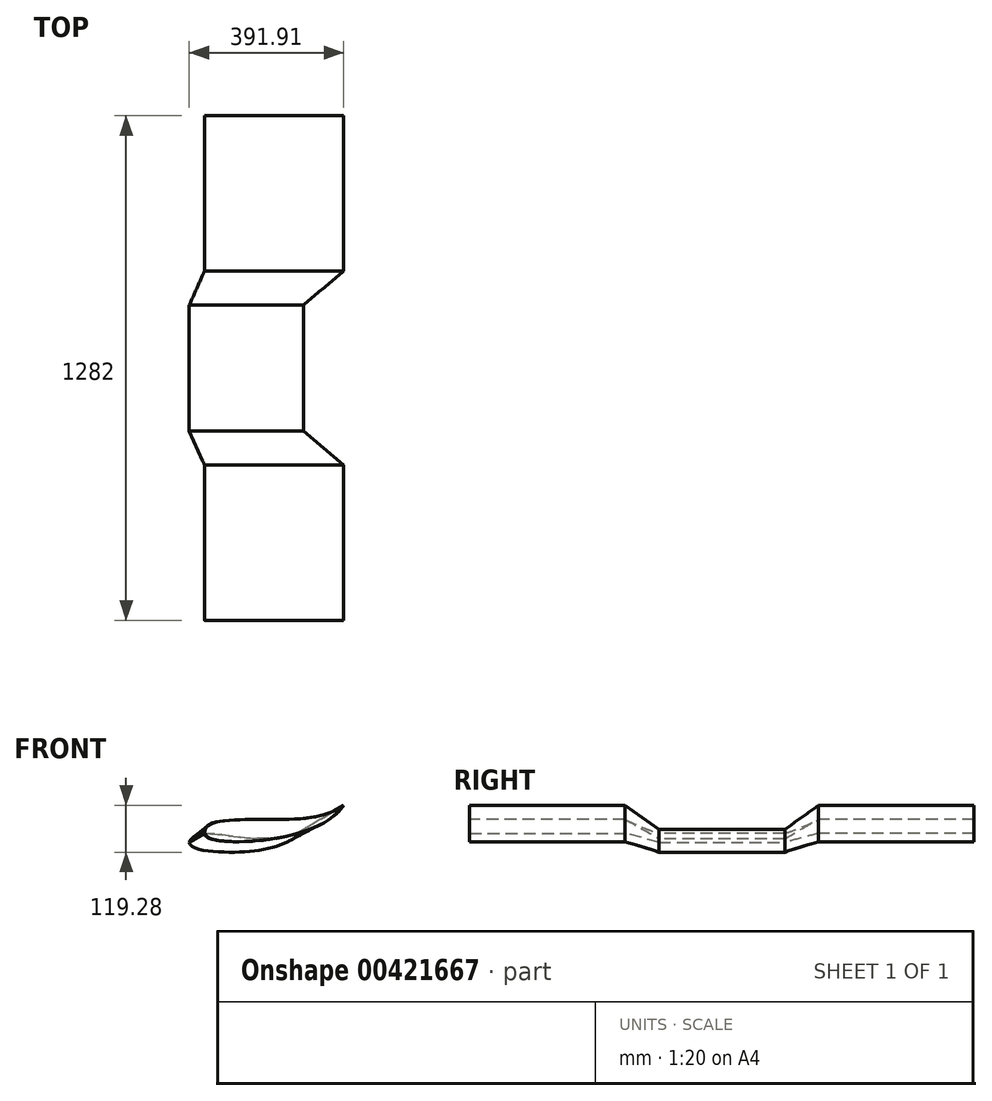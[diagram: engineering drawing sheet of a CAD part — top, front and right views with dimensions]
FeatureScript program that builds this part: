
annotation { "Feature Type Name" : "Feature", "Feature Type Description" : "" }
export const myFeature = defineFeature(function(context is Context, id is Id, definition is map)
    precondition{}
    {
        {
            var Q0;
            Q0=qCreatedBy(makeId("Front.planeOp"),FACE);
            var sketch = newSketch(context, id + "F0", { "sketchPlane" : qUnion([Q0])});
            skFitSpline(sketch, "E0", {"points": [v(-1480, 56.15) * mm, v(-1419.48, 77.77) * mm, v(-1335.27, 67.16) * mm, v(-1190, 88.73) * mm], "startDerivative": vector(83.33, 235.86) * mm, "endDerivative": vector(297.26, 176.86) * mm});
            skFitSpline(sketch, "E1", {"points": [v(-1480, 56.15) * mm, v(-1403.2, 31.78) * mm, v(-1273, 41.68) * mm, v(-1190, 88.73) * mm], "startDerivative": vector(25.78, -171.96) * mm, "endDerivative": vector(246.65, 254.9) * mm});
            skSolve(sketch);
        }
        {
            var Q0;
            Q0=makeQuery(id+"F0.imprint","IMPRINT",FACE,{"disambiguationData":[TD([[makeQuery(id+"F0.imprint","IMPRINT",EDGE,{"derivedFrom":sQuery(id+"F0.wireOp",EDGE,"E0")}),-1.0]])]});
            extrude(context, id + "F1", {"entities" : qUnion([Q0]), "depth" : 160 * mm});
        }
        {
            var Q0;
            Q0=makeQuery(id+"F1.opExtrude","CAP_FACE",FACE,{"disambiguationData":[OSD([sQuery(id+"F0.wireOp",EDGE,"E0"),sQuery(id+"F0.wireOp",EDGE,"E1")])],"isStart":false});
            cPlane(context, id + "F2", {"entities" : qUnion([Q0]), "cplaneType" : CPlaneType.OFFSET, "offset" : 86 * mm, "width" : 150 * mm, "height" : 150 * mm});
        }
        {
            var Q0;
            Q0=qCreatedBy(id+"F2.planeOp",FACE);
            var sketch = newSketch(context, id + "F3", { "sketchPlane" : qUnion([Q0])});
            skFitSpline(sketch, "E2", {"points": [v(-1441.44, 79.28) * mm, v(-1416.62, 106.26) * mm, v(-1219.62, 114.8) * mm, v(-1088.09, 150.3) * mm], "startDerivative": vector(-10.19, 203.74) * mm, "endDerivative": vector(242.21, 191.2) * mm});
            skFitSpline(sketch, "E3", {"points": [v(-1441.44, 79.28) * mm, v(-1323.8, 58.86) * mm, v(-1159.15, 95.59) * mm, v(-1088.09, 150.3) * mm], "startDerivative": vector(19.08, -187.2) * mm, "endDerivative": vector(157.9, 247.64) * mm});
            skSolve(sketch);
        }
        {
            var Q0;
            Q0=makeQuery(id+"F3.imprint","IMPRINT",FACE,{"disambiguationData":[TD([[makeQuery(id+"F3.imprint","IMPRINT",EDGE,{"derivedFrom":sQuery(id+"F3.wireOp",EDGE,"E2")}),-1.0]])]});
            extrude(context, id + "F4", {"entities" : qUnion([Q0]), "depth" : 395 * mm});
        }
        {
            var Q0;
            Q0=makeQuery(id+"F1.opExtrude","CAP_FACE",FACE,{"disambiguationData":[OSD([sQuery(id+"F0.wireOp",EDGE,"E0"),sQuery(id+"F0.wireOp",EDGE,"E1")])],"isStart":false});
            var Q1;
            Q1=makeQuery(id+"F4.opExtrude","CAP_FACE",FACE,{"disambiguationData":[OSD([sQuery(id+"F3.wireOp",EDGE,"E2"),sQuery(id+"F3.wireOp",EDGE,"E3")])],"isStart":true});
            loft(context, id + "F5", {"operationType" : NewBodyOperationType.ADD, "sheetProfilesArray" : [{ "sheetProfileEntities" : qUnion([Q0]) }, { "sheetProfileEntities" : qUnion([Q1]) }]});
        }
        {
            var Q0;
            Q0=makeQuery(id+"F1.opExtrude","SWEPT_BODY",BODY,{"disambiguationData":[OSD([sQuery(id+"F0.wireOp",EDGE,"E0"),sQuery(id+"F0.wireOp",EDGE,"E1")])]});
            var Q1;
            Q1=makeQuery(id+"F1.opExtrude","CAP_FACE",FACE,{"disambiguationData":[OSD([sQuery(id+"F0.wireOp",EDGE,"E0"),sQuery(id+"F0.wireOp",EDGE,"E1")])],"isStart":true});
            mirror(context, id + "F6", {"operationType" : NewBodyOperationType.ADD, "entities" : qUnion([Q0]), "mirrorPlane" : qUnion([Q1])});
        }
    });
